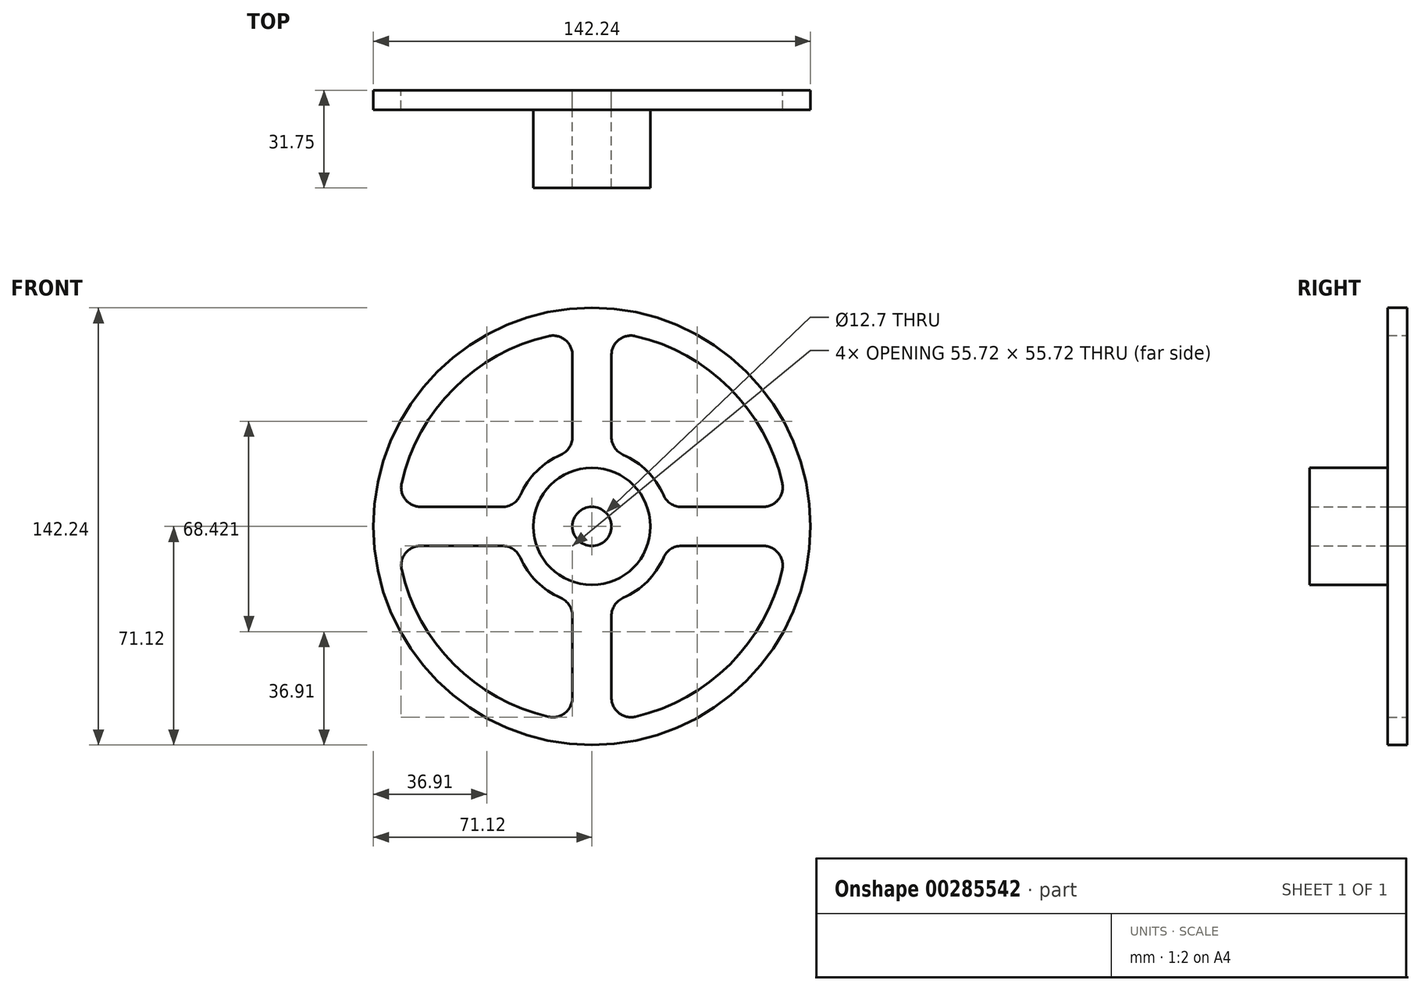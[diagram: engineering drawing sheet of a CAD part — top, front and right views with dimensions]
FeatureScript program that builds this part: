
annotation { "Feature Type Name" : "Feature", "Feature Type Description" : "" }
export const myFeature = defineFeature(function(context is Context, id is Id, definition is map)
    precondition{}
    {
        {
            var Q0;
            Q0=qCreatedBy(makeId("Front.planeOp"),FACE);
            var sketch = newSketch(context, id + "F0", { "sketchPlane" : qUnion([Q0])});
            skPoint(sketch, "E0", {"position": v(0, 0) * mm});
            skCircle(sketch, "E1", {"center": v(0, 0) * mm, "radius": 71.12 * mm});
            skArc(sketch, "E2", {"start": v(61.91, 14.11) * mm, "mid": v(44.9, 44.9) * mm, "end": v(14.11, 61.91) * mm});
            skArc(sketch, "E3", {"start": v(23.28, 10.16) * mm, "mid": v(17.96, 17.96) * mm, "end": v(10.16, 23.28) * mm});
            skCircle(sketch, "E4", {"center": v(0, 0) * mm, "radius": 19.05 * mm});
            skCircle(sketch, "E5", {"center": v(0, 0) * mm, "radius": 6.35 * mm});
            skLineSegment(sketch, "E6", {"start": v(-29.1, 6.35) * mm, "end": v(-55.72, 6.35) * mm});
            skLineSegment(sketch, "E7", {"start": v(29.1, 6.35) * mm, "end": v(55.72, 6.35) * mm});
            skLineSegment(sketch, "E8.0", {"start": v(-29.1, -6.35) * mm, "end": v(-55.72, -6.35) * mm});
            skLineSegment(sketch, "E8.1", {"start": v(29.1, -6.35) * mm, "end": v(55.72, -6.35) * mm});
            skLineSegment(sketch, "E9", {"start": v(-6.35, 29.1) * mm, "end": v(-6.35, 55.72) * mm});
            skLineSegment(sketch, "E10", {"start": v(-6.35, -29.1) * mm, "end": v(-6.35, -55.72) * mm});
            skLineSegment(sketch, "E11", {"start": v(6.35, -24.6) * mm, "end": v(6.35, -63.18) * mm});
            skLineSegment(sketch, "E12", {"start": v(6.35, -55.72) * mm, "end": v(6.35, -29.1) * mm});
            skPoint(sketch, "E13.orphan", {"position": v(-6.35, 0) * mm});
            skLineSegment(sketch, "E14.trimOffspring", {"start": v(6.35, 29.1) * mm, "end": v(6.35, 55.72) * mm});
            skPoint(sketch, "E15.orphan", {"position": v(6.35, 0) * mm});
            skPoint(sketch, "E16.orphan", {"position": v(0, 6.35) * mm});
            skArc(sketch, "E17.trimOffspring", {"start": v(-10.16, 23.28) * mm, "mid": v(-17.96, 17.96) * mm, "end": v(-23.28, 10.16) * mm});
            skArc(sketch, "E18.trimOffspring", {"start": v(-23.28, -10.16) * mm, "mid": v(-17.96, -17.96) * mm, "end": v(-10.16, -23.28) * mm});
            skArc(sketch, "E19.trimOffspring", {"start": v(10.16, -23.28) * mm, "mid": v(17.96, -17.96) * mm, "end": v(23.28, -10.16) * mm});
            skArc(sketch, "E20.trimOffspring", {"start": v(-61.91, -14.11) * mm, "mid": v(-44.9, -44.9) * mm, "end": v(-14.11, -61.91) * mm});
            skArc(sketch, "E21.trimOffspring", {"start": v(14.11, -61.91) * mm, "mid": v(44.9, -44.9) * mm, "end": v(61.91, -14.11) * mm});
            skArc(sketch, "E22.trimOffspring", {"start": v(-14.11, 61.91) * mm, "mid": v(-44.9, 44.9) * mm, "end": v(-61.91, 14.11) * mm});
            skPoint(sketch, "E23.visualSharp", {"position": v(6.35, 24.6) * mm});
            skArc(sketch, "E23.filletArc", {"start": v(6.35, 29.1) * mm, "mid": v(7.39, 25.62) * mm, "end": v(10.16, 23.28) * mm});
            skPoint(sketch, "E24.visualSharp", {"position": v(6.35, 63.18) * mm});
            skArc(sketch, "E24.filletArc", {"start": v(14.11, 61.91) * mm, "mid": v(8.74, 60.69) * mm, "end": v(6.35, 55.72) * mm});
            skPoint(sketch, "E25.visualSharp", {"position": v(63.18, 6.35) * mm});
            skArc(sketch, "E25.filletArc", {"start": v(55.72, 6.35) * mm, "mid": v(60.69, 8.74) * mm, "end": v(61.91, 14.11) * mm});
            skPoint(sketch, "E26.visualSharp", {"position": v(24.6, 6.35) * mm});
            skArc(sketch, "E26.filletArc", {"start": v(23.28, 10.16) * mm, "mid": v(25.62, 7.39) * mm, "end": v(29.1, 6.35) * mm});
            skPoint(sketch, "E27.visualSharp", {"position": v(24.6, -6.35) * mm});
            skArc(sketch, "E27.filletArc", {"start": v(29.1, -6.35) * mm, "mid": v(25.62, -7.39) * mm, "end": v(23.28, -10.16) * mm});
            skPoint(sketch, "E28.visualSharp", {"position": v(63.18, -6.35) * mm});
            skArc(sketch, "E28.filletArc", {"start": v(61.91, -14.11) * mm, "mid": v(60.69, -8.74) * mm, "end": v(55.72, -6.35) * mm});
            skPoint(sketch, "E29.visualSharp", {"position": v(6.35, -63.18) * mm});
            skArc(sketch, "E29.filletArc", {"start": v(6.35, -55.72) * mm, "mid": v(8.74, -60.69) * mm, "end": v(14.11, -61.91) * mm});
            skPoint(sketch, "E30.visualSharp", {"position": v(6.35, -24.6) * mm});
            skArc(sketch, "E30.filletArc", {"start": v(10.16, -23.28) * mm, "mid": v(7.39, -25.62) * mm, "end": v(6.35, -29.1) * mm});
            skPoint(sketch, "E31.visualSharp", {"position": v(-6.35, -24.6) * mm});
            skArc(sketch, "E31.filletArc", {"start": v(-6.35, -29.1) * mm, "mid": v(-7.39, -25.62) * mm, "end": v(-10.16, -23.28) * mm});
            skPoint(sketch, "E32.visualSharp", {"position": v(-24.6, -6.35) * mm});
            skArc(sketch, "E32.filletArc", {"start": v(-23.28, -10.16) * mm, "mid": v(-25.62, -7.39) * mm, "end": v(-29.1, -6.35) * mm});
            skPoint(sketch, "E33.visualSharp", {"position": v(-63.18, -6.35) * mm});
            skArc(sketch, "E33.filletArc", {"start": v(-55.72, -6.35) * mm, "mid": v(-60.69, -8.74) * mm, "end": v(-61.91, -14.11) * mm});
            skPoint(sketch, "E34.visualSharp", {"position": v(-6.35, -63.18) * mm});
            skArc(sketch, "E34.filletArc", {"start": v(-14.11, -61.91) * mm, "mid": v(-8.74, -60.69) * mm, "end": v(-6.35, -55.72) * mm});
            skPoint(sketch, "E35.visualSharp", {"position": v(-24.6, 6.35) * mm});
            skArc(sketch, "E35.filletArc", {"start": v(-29.1, 6.35) * mm, "mid": v(-25.62, 7.39) * mm, "end": v(-23.28, 10.16) * mm});
            skPoint(sketch, "E36.visualSharp", {"position": v(-6.35, 24.6) * mm});
            skArc(sketch, "E36.filletArc", {"start": v(-10.16, 23.28) * mm, "mid": v(-7.39, 25.62) * mm, "end": v(-6.35, 29.1) * mm});
            skPoint(sketch, "E37.visualSharp", {"position": v(-6.35, 63.18) * mm});
            skArc(sketch, "E37.filletArc", {"start": v(-6.35, 55.72) * mm, "mid": v(-8.74, 60.69) * mm, "end": v(-14.11, 61.91) * mm});
            skPoint(sketch, "E38.visualSharp", {"position": v(-63.18, 6.35) * mm});
            skArc(sketch, "E38.filletArc", {"start": v(-61.91, 14.11) * mm, "mid": v(-60.69, 8.74) * mm, "end": v(-55.72, 6.35) * mm});
            skSolve(sketch);
        }
        {
            var Q0;
            Q0 = qSketchRegion(id + "F0", true);
            extrude(context, id + "F1", {"entities" : qUnion([Q0]), "depth" : 6.35 * mm});
        }
        {
            var Q0;
            Q0=makeQuery(id+"F0.imprint","IMPRINT",FACE,{"disambiguationData":[TD([[makeQuery(id+"F0.imprint","IMPRINT",EDGE,{"derivedFrom":sQuery(id+"F0.wireOp",EDGE,"E4")}),1.0]])]});
            extrude(context, id + "F2", {"entities" : qUnion([Q0]), "operationType" : NewBodyOperationType.ADD, "depth" : 31.75 * mm});
        }
    });
